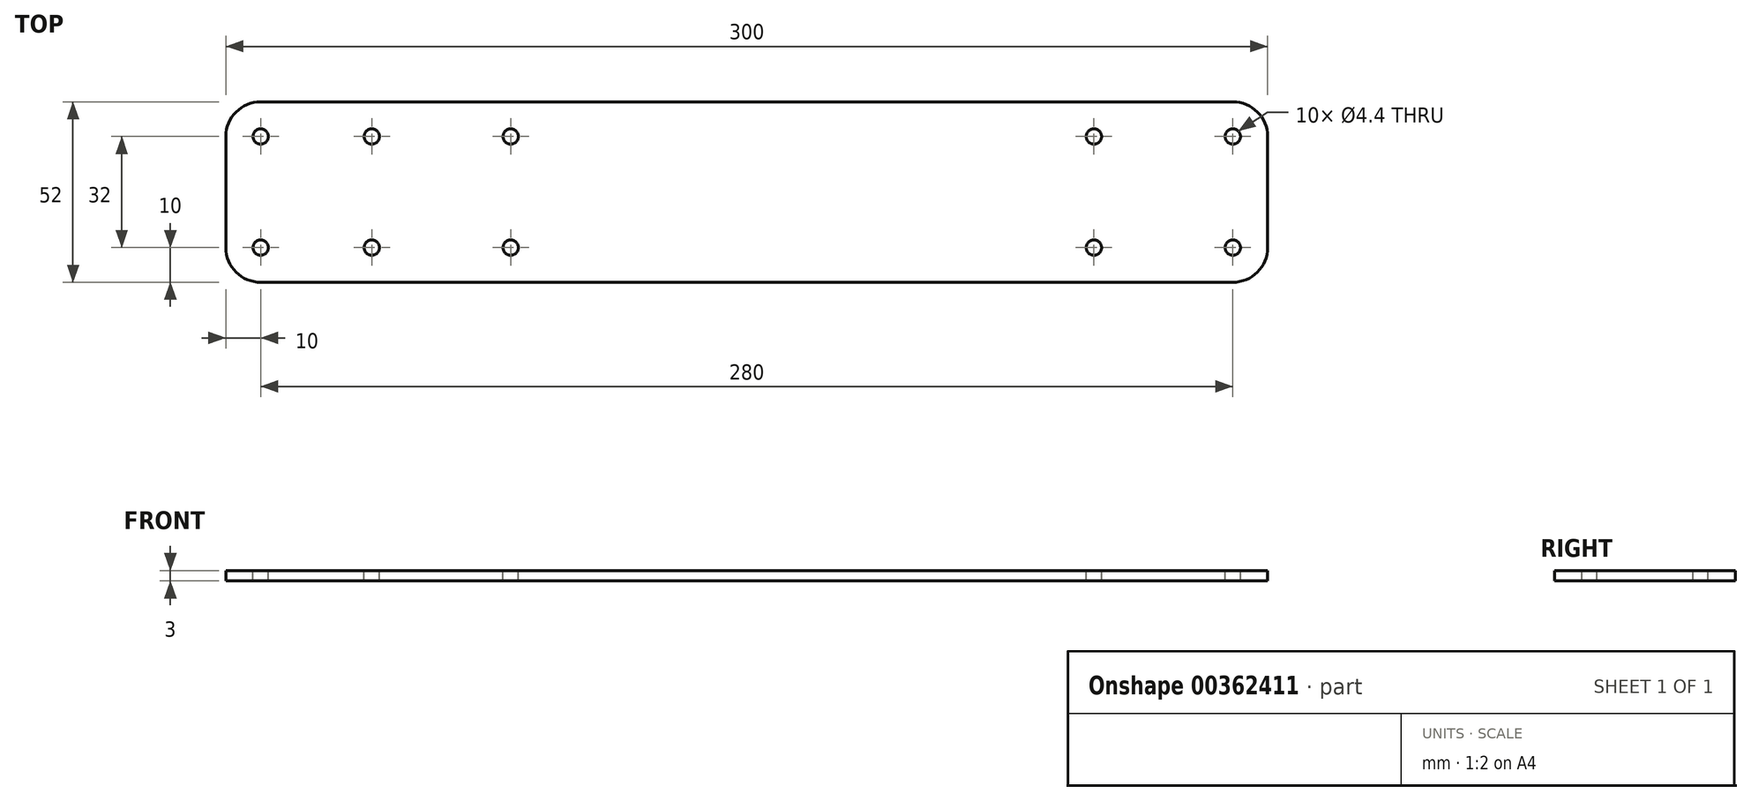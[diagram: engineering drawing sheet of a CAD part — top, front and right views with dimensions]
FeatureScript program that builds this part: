
annotation { "Feature Type Name" : "Feature", "Feature Type Description" : "" }
export const myFeature = defineFeature(function(context is Context, id is Id, definition is map)
    precondition{}
    {
        {
            var Q0;
            Q0=qCreatedBy(makeId("Top.planeOp"),FACE);
            var sketch = newSketch(context, id + "F0", { "sketchPlane" : qUnion([Q0])});
            skLineSegment(sketch, "E0.bottom", {"start": v(140, -26) * mm, "end": v(-140, -26) * mm});
            skLineSegment(sketch, "E0.top", {"start": v(140, 26) * mm, "end": v(-140, 26) * mm});
            skLineSegment(sketch, "E0.left", {"start": v(150, -16) * mm, "end": v(150, 16) * mm});
            skLineSegment(sketch, "E0.right", {"start": v(-150, -16) * mm, "end": v(-150, 16) * mm});
            skPoint(sketch, "E0.middle", {"position": v(0, 0) * mm});
            skPoint(sketch, "E1.visualSharp", {"position": v(-150, 26) * mm});
            skArc(sketch, "E1.filletArc", {"start": v(-140, 26) * mm, "mid": v(-147.07, 23.07) * mm, "end": v(-150, 16) * mm});
            skPoint(sketch, "E2.visualSharp", {"position": v(-150, -26) * mm});
            skArc(sketch, "E2.filletArc", {"start": v(-150, -16) * mm, "mid": v(-147.07, -23.07) * mm, "end": v(-140, -26) * mm});
            skPoint(sketch, "E3.visualSharp", {"position": v(150, -26) * mm});
            skArc(sketch, "E3.filletArc", {"start": v(140, -26) * mm, "mid": v(147.07, -23.07) * mm, "end": v(150, -16) * mm});
            skPoint(sketch, "E4.visualSharp", {"position": v(150, 26) * mm});
            skArc(sketch, "E4.filletArc", {"start": v(150, 16) * mm, "mid": v(147.07, 23.07) * mm, "end": v(140, 26) * mm});
            skSolve(sketch);
        }
        {
            var Q0;
            Q0=makeQuery(id+"F0.imprint","IMPRINT",FACE,{"disambiguationData":[TD([[makeQuery(id+"F0.imprint","IMPRINT",EDGE,{"derivedFrom":sQuery(id+"F0.wireOp",EDGE,"E0.bottom")}),-1.0]])]});
            extrude(context, id + "F1", {"entities" : qUnion([Q0]), "depth" : 3 * mm});
        }
        {
            var Q0;
            Q0=makeQuery(id+"F1.opExtrude","CAP_FACE",FACE,{"disambiguationData":[OSD([sQuery(id+"F0.wireOp",EDGE,"E0.bottom"),sQuery(id+"F0.wireOp",EDGE,"E0.top"),sQuery(id+"F0.wireOp",EDGE,"E0.left"),sQuery(id+"F0.wireOp",EDGE,"E0.right"),sQuery(id+"F0.wireOp",EDGE,"E1.filletArc"),sQuery(id+"F0.wireOp",EDGE,"E2.filletArc"),sQuery(id+"F0.wireOp",EDGE,"E3.filletArc"),sQuery(id+"F0.wireOp",EDGE,"E4.filletArc")])],"isStart":false});
            var sketch = newSketch(context, id + "F2", { "sketchPlane" : qUnion([Q0])});
            skPoint(sketch, "E5", {"position": v(-140, 16) * mm});
            skLineSegment(sketch, "E6", {"start": v(0, 26) * mm, "end": v(0, -26) * mm});
            skPoint(sketch, "E7.0.1.0", {"position": v(-140, -16) * mm});
            skPoint(sketch, "E7.1.0.0", {"position": v(-108, 16) * mm});
            skPoint(sketch, "E7.1.1.0", {"position": v(-108, -16) * mm});
            skLineSegment(sketch, "E7.direction1", {"start": v(-140, 16) * mm, "end": v(-108, 16) * mm, "construction": true});
            skLineSegment(sketch, "E7.direction2", {"start": v(-140, 16) * mm, "end": v(-140, -16) * mm, "construction": true});
            skPoint(sketch, "E8", {"position": v(140, 16) * mm});
            skPoint(sketch, "E9.0.1.0", {"position": v(140, -16) * mm});
            skPoint(sketch, "E9.1.0.0", {"position": v(100, 16) * mm});
            skPoint(sketch, "E9.1.1.0", {"position": v(100, -16) * mm});
            skLineSegment(sketch, "E9.direction1", {"start": v(140, 16) * mm, "end": v(100, 16) * mm, "construction": true});
            skLineSegment(sketch, "E9.direction2", {"start": v(140, 16) * mm, "end": v(140, -16) * mm, "construction": true});
            skPoint(sketch, "E10", {"position": v(-68, 16) * mm});
            skPoint(sketch, "E11.0.1.0", {"position": v(-68, -16) * mm});
            skLineSegment(sketch, "E11.direction2", {"start": v(-68, 16) * mm, "end": v(-68, -16) * mm, "construction": true});
            skSolve(sketch);
        }
        {
            var Q0;
            Q0=sQuery(id+"F2.wireOp",VERTEX,"E5");
            var Q1;
            Q1=sQuery(id+"F2.wireOp",VERTEX,"E7.0.1.0");
            var Q2;
            Q2=sQuery(id+"F2.wireOp",VERTEX,"E7.1.1.0");
            var Q3;
            Q3=sQuery(id+"F2.wireOp",VERTEX,"E7.1.0.0");
            var Q4;
            Q4=sQuery(id+"F2.wireOp",VERTEX,"E10");
            var Q5;
            Q5=sQuery(id+"F2.wireOp",VERTEX,"E11.0.1.0");
            var Q6;
            Q6=sQuery(id+"F2.wireOp",VERTEX,"E8");
            var Q7;
            Q7=sQuery(id+"F2.wireOp",VERTEX,"E9.1.0.0");
            var Q8;
            Q8=sQuery(id+"F2.wireOp",VERTEX,"E9.1.1.0");
            var Q9;
            Q9=sQuery(id+"F2.wireOp",VERTEX,"E9.0.1.0");
            var Q10;
            Q10=makeQuery(id+"F1.opExtrude","SWEPT_BODY",BODY,{"disambiguationData":[OSD([sQuery(id+"F0.wireOp",EDGE,"E0.bottom"),sQuery(id+"F0.wireOp",EDGE,"E0.top"),sQuery(id+"F0.wireOp",EDGE,"E0.left"),sQuery(id+"F0.wireOp",EDGE,"E0.right"),sQuery(id+"F0.wireOp",EDGE,"E1.filletArc"),sQuery(id+"F0.wireOp",EDGE,"E2.filletArc"),sQuery(id+"F0.wireOp",EDGE,"E3.filletArc"),sQuery(id+"F0.wireOp",EDGE,"E4.filletArc")])]});
            hole(context, id + "F3", {"style" : HoleStyle.SIMPLE, "endStyle" : HoleEndStyle.THROUGH, "standardTappedOrClearance" : lookupTablePath({ "standard" : "ISO", "fit" : "Normal", "size" : "M4", "type" : "Clearance" }), "standardBlindInLast" : lookupTablePath({ "fit" : "Standard", "standard" : "ISO", "size" : "M4", "type" : "Clearance" }), "holeDiameter" : 4.4 * mm, "locations" : qUnion([Q0, Q1, Q2, Q3, Q4, Q5, Q6, Q7, Q8, Q9]), "scope" : qUnion([Q10]), "isTappedThrough" : true});
        }
    });
